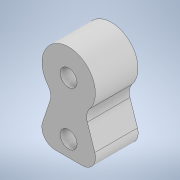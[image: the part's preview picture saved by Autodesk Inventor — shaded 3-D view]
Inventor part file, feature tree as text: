
AUTODESK INVENTOR PART (.ipt)
format: ipt  version: 2022 (Build 260153000, 153)  size: 135,168 bytes
history: native  units: in
note: dims shown in document units (in); Inventor stores cm internally (conversion verified against a paired STEP export)
features: extrude x2, sketch x1, fillet x1
ambient origin geometry x8: Origin, YZ Plane, XZ Plane, XY Plane, X Axis, Y Axis, Z Axis, Center Point
bodies: Solid1 (feature_tree)
feature tree (4):
  sketch  "Sketch1"  dims[d0=0.079in d1=0.25in d2=0.15in d3=0.079in d4=0.225in d5=0.075in d6=0.2in d7=0.0in d10=0.075in d11=0.075in d12=0.2in d13=0.0in d14=0.0625in]
  extrude  "Extrusion1"  Depth=0.25in
  extrude  "Extrusion3"  Depth=0.0625in
  fillet  "Fillet1"  Radius=0.079in
